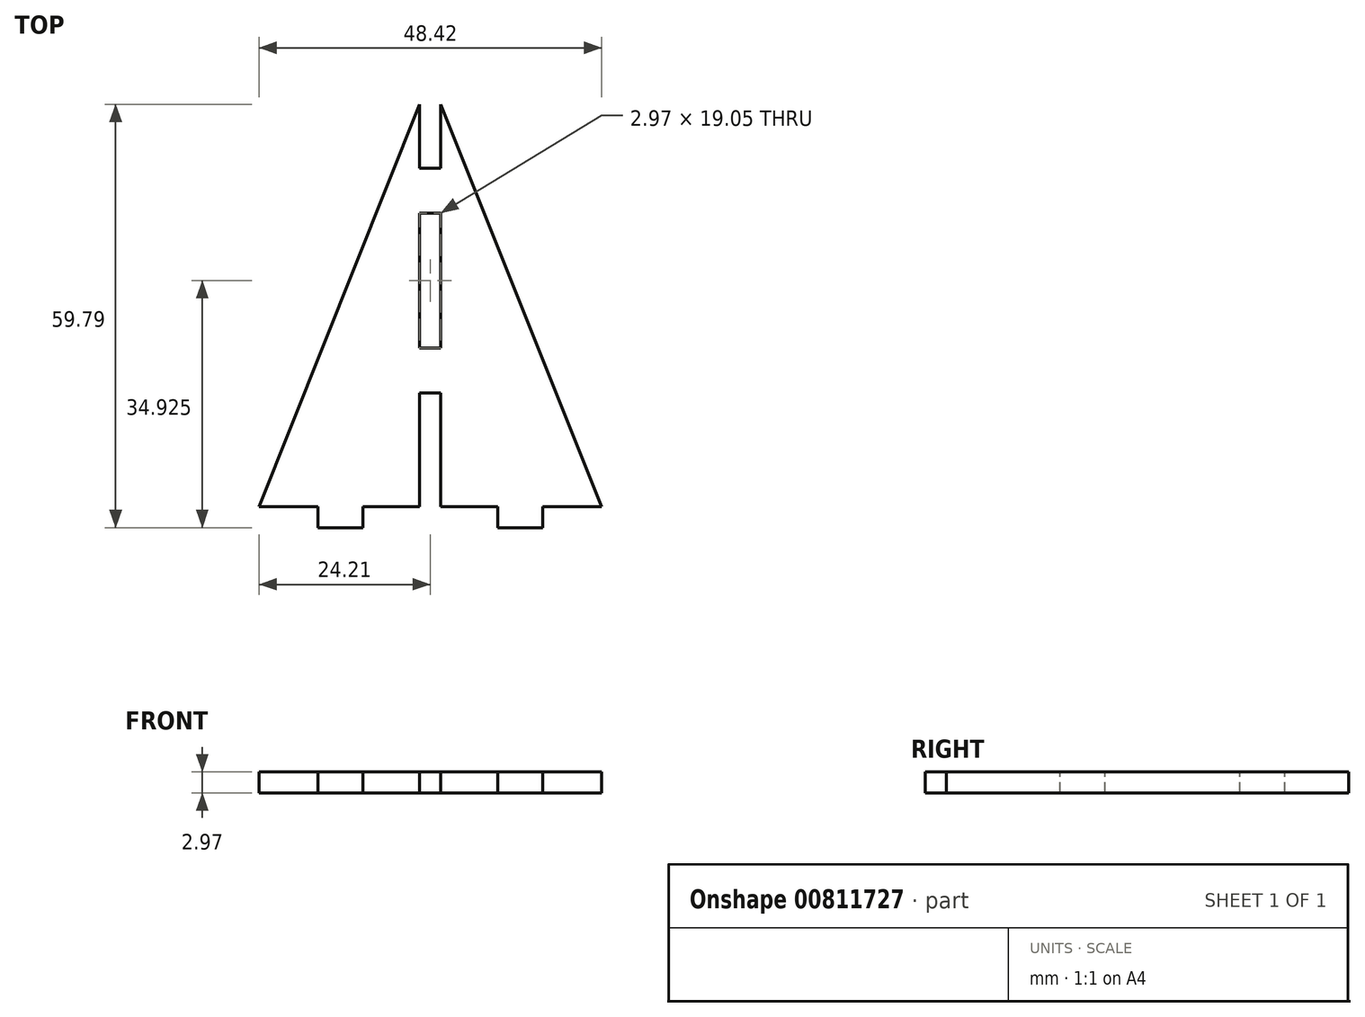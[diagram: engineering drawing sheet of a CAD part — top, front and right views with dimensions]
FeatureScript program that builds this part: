
annotation { "Feature Type Name" : "Feature", "Feature Type Description" : "" }
export const myFeature = defineFeature(function(context is Context, id is Id, definition is map)
    precondition{}
    {
        {
            var Q0;
            Q0=qCreatedBy(makeId("Top.planeOp"),FACE);
            var sketch = newSketch(context, id + "F0", { "sketchPlane" : qUnion([Q0])});
            skLineSegment(sketch, "E0", {"start": v(0, 63.5) * mm, "end": v(-25.4, 0) * mm});
            skLineSegment(sketch, "E1", {"start": v(-25.4, 0) * mm, "end": v(25.4, 0) * mm});
            skLineSegment(sketch, "E2", {"start": v(25.4, 0) * mm, "end": v(0, 63.5) * mm});
            skSolve(sketch);
        }
        {
            var Q0;
            Q0 = qSketchRegion(id + "F0", true);
            extrude(context, id + "F1", {"entities" : qUnion([Q0]), "depth" : 2.97 * mm, "offsetDistance" : 25.4 * mm});
        }
        {
            var Q0;
            Q0=makeQuery(id+"F1.opExtrude","CAP_FACE",FACE,{"disambiguationData":[OSD([sQuery(id+"F0.wireOp",EDGE,"E0"),sQuery(id+"F0.wireOp",EDGE,"E1"),sQuery(id+"F0.wireOp",EDGE,"E2")])],"isStart":false});
            var sketch = newSketch(context, id + "F2", { "sketchPlane" : qUnion([Q0])});
            skLineSegment(sketch, "E3.bottom", {"start": v(1.49, 0) * mm, "end": v(-1.49, 0) * mm});
            skLineSegment(sketch, "E3.top", {"start": v(1.49, 19.05) * mm, "end": v(-1.49, 19.05) * mm});
            skLineSegment(sketch, "E3.left", {"start": v(1.49, 0) * mm, "end": v(1.49, 19.05) * mm});
            skLineSegment(sketch, "E3.right", {"start": v(-1.49, 0) * mm, "end": v(-1.49, 19.05) * mm});
            skPoint(sketch, "E3.middle", {"position": v(0, 9.53) * mm});
            skLineSegment(sketch, "E4.bottom", {"start": v(1.49, 25.4) * mm, "end": v(-1.49, 25.4) * mm});
            skLineSegment(sketch, "E4.top", {"start": v(1.49, 44.45) * mm, "end": v(-1.49, 44.45) * mm});
            skLineSegment(sketch, "E4.left", {"start": v(1.49, 25.4) * mm, "end": v(1.49, 44.45) * mm});
            skLineSegment(sketch, "E4.right", {"start": v(-1.49, 25.4) * mm, "end": v(-1.49, 44.45) * mm});
            skPoint(sketch, "E4.middle", {"position": v(0, 34.92) * mm});
            skPoint(sketch, "E4.cornerSnap0", {"position": v(1.49, 9.53) * mm});
            skLineSegment(sketch, "E5.bottom", {"start": v(1.49, 50.8) * mm, "end": v(-1.49, 50.8) * mm});
            skLineSegment(sketch, "E5.top", {"start": v(1.49, 76.2) * mm, "end": v(-1.49, 76.2) * mm});
            skLineSegment(sketch, "E5.left", {"start": v(1.49, 50.8) * mm, "end": v(1.49, 76.2) * mm});
            skLineSegment(sketch, "E5.right", {"start": v(-1.49, 50.8) * mm, "end": v(-1.49, 76.2) * mm});
            skPoint(sketch, "E5.middle", {"position": v(0, 63.5) * mm});
            skSolve(sketch);
        }
        {
            var Q0;
            Q0 = qSketchRegion(id + "F2", true);
            extrude(context, id + "F3", {"entities" : qUnion([Q0]), "operationType" : NewBodyOperationType.REMOVE, "oppositeDirection" : true, "depth" : 25.4 * mm, "offsetDistance" : 25.4 * mm});
        }
        {
            var Q0;
            Q0=makeQuery(id+"F1.opExtrude","CAP_FACE",FACE,{"disambiguationData":[OSD([sQuery(id+"F0.wireOp",EDGE,"E0"),sQuery(id+"F0.wireOp",EDGE,"E1"),sQuery(id+"F0.wireOp",EDGE,"E2")])],"isStart":false});
            var sketch = newSketch(context, id + "F4", { "sketchPlane" : qUnion([Q0])});
            skLineSegment(sketch, "E6.bottom", {"start": v(-1.49, 0) * mm, "end": v(-9.53, 0) * mm});
            skLineSegment(sketch, "E6.top", {"start": v(-1.49, 2.97) * mm, "end": v(-9.53, 2.97) * mm});
            skLineSegment(sketch, "E6.left", {"start": v(-1.49, 0) * mm, "end": v(-1.49, 2.97) * mm});
            skLineSegment(sketch, "E6.right", {"start": v(-9.53, 0) * mm, "end": v(-9.53, 2.97) * mm});
            skLineSegment(sketch, "E7.bottom", {"start": v(-15.88, 0) * mm, "end": v(-28.58, 0) * mm});
            skLineSegment(sketch, "E7.top", {"start": v(-15.88, 2.97) * mm, "end": v(-28.58, 2.97) * mm});
            skLineSegment(sketch, "E7.left", {"start": v(-15.88, 0) * mm, "end": v(-15.88, 2.97) * mm});
            skLineSegment(sketch, "E7.right", {"start": v(-28.58, 0) * mm, "end": v(-28.58, 2.97) * mm});
            skLineSegment(sketch, "E8.bottom", {"start": v(1.49, 0) * mm, "end": v(9.53, 0) * mm});
            skLineSegment(sketch, "E8.top", {"start": v(1.49, 2.97) * mm, "end": v(9.53, 2.97) * mm});
            skLineSegment(sketch, "E8.left", {"start": v(1.49, 0) * mm, "end": v(1.49, 2.97) * mm});
            skLineSegment(sketch, "E8.right", {"start": v(9.53, 0) * mm, "end": v(9.53, 2.97) * mm});
            skLineSegment(sketch, "E9.bottom", {"start": v(15.88, 0) * mm, "end": v(28.58, 0) * mm});
            skLineSegment(sketch, "E9.top", {"start": v(15.88, 2.97) * mm, "end": v(28.58, 2.97) * mm});
            skLineSegment(sketch, "E9.left", {"start": v(15.88, 0) * mm, "end": v(15.88, 2.97) * mm});
            skLineSegment(sketch, "E9.right", {"start": v(28.58, 0) * mm, "end": v(28.58, 2.97) * mm});
            skSolve(sketch);
        }
        {
            var Q0;
            Q0 = qSketchRegion(id + "F4", true);
            extrude(context, id + "F5", {"entities" : qUnion([Q0]), "operationType" : NewBodyOperationType.REMOVE, "oppositeDirection" : true, "depth" : 25.4 * mm, "offsetDistance" : 25.4 * mm});
        }
    });
